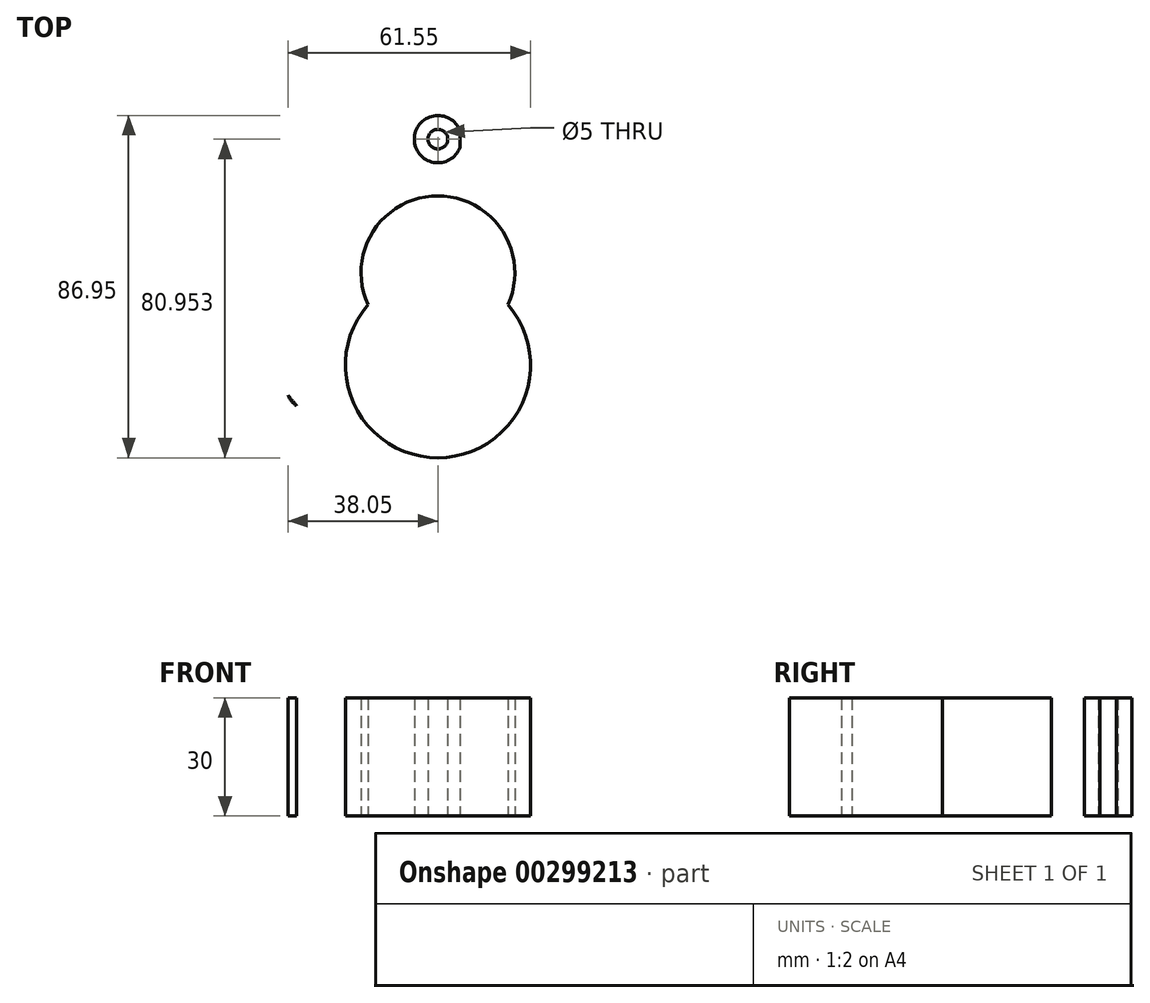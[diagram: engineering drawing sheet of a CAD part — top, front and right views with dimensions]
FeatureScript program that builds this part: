
annotation { "Feature Type Name" : "Feature", "Feature Type Description" : "" }
export const myFeature = defineFeature(function(context is Context, id is Id, definition is map)
    precondition{}
    {
        {
            var Q0;
            Q0=qCreatedBy(makeId("Top.planeOp"),FACE);
            var sketch = newSketch(context, id + "F0", { "sketchPlane" : qUnion([Q0])});
            skCircle(sketch, "E0", {"center": v(0, 0) * mm, "radius": 13 * mm});
            skCircle(sketch, "E1", {"center": v(0, 0) * mm, "radius": 20 * mm});
            skCircle(sketch, "E2", {"center": v(0, 0) * mm, "radius": 23.5 * mm});
            skArc(sketch, "E3", {"start": v(17.77, 15.38) * mm, "mid": v(0, 43.04) * mm, "end": v(-17.77, 15.38) * mm});
            skCircle(sketch, "E4", {"center": v(0, 23.5) * mm, "radius": 14.54 * mm});
            skCircle(sketch, "E5", {"center": v(-32.5, -5.34) * mm, "radius": 6 * mm});
            skPoint(sketch, "E6.orphan", {"position": v(0, -7.55) * mm});
            skCircle(sketch, "E7", {"center": v(-32.5, -5.34) * mm, "radius": 2.5 * mm});
            skCircle(sketch, "E8", {"center": v(32.5, -5.69) * mm, "radius": 6 * mm});
            skCircle(sketch, "E9", {"center": v(32.5, -5.69) * mm, "radius": 2.5 * mm});
            skCircle(sketch, "E10", {"center": v(0, 57.45) * mm, "radius": 6 * mm});
            skCircle(sketch, "E11", {"center": v(0, 57.45) * mm, "radius": 2.5 * mm});
            skLineSegment(sketch, "E12", {"start": v(5.6, 59.59) * mm, "end": v(5.6, 42.22) * mm});
            skLineSegment(sketch, "E13", {"start": v(-6, 57.45) * mm, "end": v(-6, 42.1) * mm});
            skLineSegment(sketch, "E14", {"start": v(-32.5, -5.34) * mm, "end": v(-30.84, -5.69) * mm, "construction": true});
            skLineSegment(sketch, "E15", {"start": v(42.3, 57.45) * mm, "end": v(-57.95, 57.45) * mm, "construction": true});
            skLineSegment(sketch, "E16", {"start": v(-2.13, 23.5) * mm, "end": v(-57.13, 23.5) * mm, "construction": true});
            skArc(sketch, "E17", {"start": v(-26.82, 24) * mm, "mid": v(-29.6, 19.39) * mm, "end": v(-30.2, 14.03) * mm});
            skLineSegment(sketch, "E18", {"start": v(-5.18, 60.47) * mm, "end": v(-26.82, 24) * mm});
            skLineSegment(sketch, "E19", {"start": v(5.6, 60.47) * mm, "end": v(28.74, 26.8) * mm});
            skLineSegment(sketch, "E20", {"start": v(-30.2, 14.03) * mm, "end": v(-37.95, -2.83) * mm});
            skLineSegment(sketch, "E21", {"start": v(31.53, 14.03) * mm, "end": v(38.12, -3.59) * mm});
            skArc(sketch, "E22", {"start": v(-38.05, -7.6) * mm, "mid": v(0.8, -26.3) * mm, "end": v(38.49, -5.34) * mm});
            skArc(sketch, "E23.trimOffspring", {"start": v(-7.37, 22.31) * mm, "mid": v(-7.8, 22.92) * mm, "end": v(-8.27, 23.5) * mm});
            skArc(sketch, "E24.trimOffspring", {"start": v(31.53, 14.03) * mm, "mid": v(31.93, 20.81) * mm, "end": v(28.74, 26.8) * mm});
            skLineSegment(sketch, "E25", {"start": v(-32.5, -11.34) * mm, "end": v(-20.59, -11.34) * mm});
            skLineSegment(sketch, "E26", {"start": v(-30.84, 0) * mm, "end": v(-23.5, 0) * mm});
            skLineSegment(sketch, "E27", {"start": v(30.6, 0) * mm, "end": v(23.5, 0) * mm});
            skLineSegment(sketch, "E28", {"start": v(30.47, -11.34) * mm, "end": v(20.59, -11.34) * mm});
            skSolve(sketch);
        }
        {
            var Q0;
            {var subQ0=sQuery(id+"F0.wireOp",EDGE,"E22");var subQ1=sQuery(id+"F0.wireOp",EDGE,"E5");var subQ2=makeQuery(id+"F0.imprint","INTERSECT",VERTEX,{"disambiguationData":[OD(0.0)],"derivedFrom":[subQ1,subQ0]});Q0=makeQuery(id+"F0.imprint","IMPRINT",FACE,{"disambiguationData":[TD([[makeQuery(id+"F0.imprint","IMPRINT",EDGE,{"disambiguationData":[TD([[subQ2,-1.0]])],"derivedFrom":subQ1}),1.0]])]});}
            var Q1;
            {var subQ0=sQuery(id+"F0.wireOp",EDGE,"E12");var subQ1=sQuery(id+"F0.wireOp",EDGE,"E10");var subQ2=makeQuery(id+"F0.imprint","INTERSECT",VERTEX,{"disambiguationData":[OD(0.0)],"derivedFrom":[subQ1,subQ0]});Q1=makeQuery(id+"F0.imprint","IMPRINT",FACE,{"disambiguationData":[TD([[makeQuery(id+"F0.imprint","IMPRINT",EDGE,{"disambiguationData":[TD([[subQ2,1.0]])],"derivedFrom":subQ1}),1.0]])]});}
            var Q2;
            {var subQ0=sQuery(id+"F0.wireOp",EDGE,"E3");var subQ3=sQuery(id+"F0.wireOp",EDGE,"E2");var subQ4=makeQuery(id+"F0.imprint","INTERSECT",VERTEX,{"disambiguationData":[OD(0.0)],"derivedFrom":[subQ3,subQ0]});Q2=makeQuery(id+"F0.imprint","IMPRINT",FACE,{"disambiguationData":[TD([[makeQuery(id+"F0.imprint","IMPRINT",EDGE,{"disambiguationData":[TD([[subQ4,-1.0]])],"derivedFrom":subQ3}),-1.0]])]});}
            var Q3;
            {var subQ3=sQuery(id+"F0.wireOp",EDGE,"E4");var subQ5=sQuery(id+"F0.wireOp",EDGE,"E1");var subQ6=makeQuery(id+"F0.imprint","INTERSECT",VERTEX,{"disambiguationData":[OD(0.0)],"derivedFrom":[subQ5,subQ3]});Q3=makeQuery(id+"F0.imprint","IMPRINT",FACE,{"disambiguationData":[TD([[makeQuery(id+"F0.imprint","IMPRINT",EDGE,{"disambiguationData":[TD([[subQ6,-1.0]])],"derivedFrom":subQ5}),-1.0]])]});}
            var Q4;
            {var subQ0=sQuery(id+"F0.wireOp",EDGE,"E2");var subQ1=makeQuery(id+"F0.imprint","IMPRINT",VERTEX,{"derivedFrom":subQ0});Q4=makeQuery(id+"F0.imprint","IMPRINT",FACE,{"disambiguationData":[TD([[makeQuery(id+"F0.imprint","IMPRINT",EDGE,{"disambiguationData":[TD([[subQ1,1.0]])],"derivedFrom":subQ0}),-1.0]])]});}
            var Q5;
            {var subQ3=sQuery(id+"F0.wireOp",EDGE,"E2");var subQ5=makeQuery(id+"F0.imprint","IMPRINT",VERTEX,{"derivedFrom":subQ3});Q5=makeQuery(id+"F0.imprint","IMPRINT",FACE,{"disambiguationData":[TD([[makeQuery(id+"F0.imprint","IMPRINT",EDGE,{"disambiguationData":[TD([[subQ5,1.0]])],"derivedFrom":subQ3}),1.0]])]});}
            var Q6;
            {var subQ0=sQuery(id+"F0.wireOp",EDGE,"E4");var subQ1=sQuery(id+"F0.wireOp",EDGE,"E0");var subQ2=makeQuery(id+"F0.imprint","INTERSECT",VERTEX,{"disambiguationData":[OD(0.0)],"derivedFrom":[subQ1,subQ0]});Q6=makeQuery(id+"F0.imprint","IMPRINT",FACE,{"disambiguationData":[TD([[makeQuery(id+"F0.imprint","IMPRINT",EDGE,{"disambiguationData":[TD([[subQ2,1.0]])],"derivedFrom":subQ1}),-1.0]])]});}
            var Q7;
            {var subQ0=sQuery(id+"F0.wireOp",EDGE,"E4");var subQ1=sQuery(id+"F0.wireOp",EDGE,"E0");var subQ2=makeQuery(id+"F0.imprint","INTERSECT",VERTEX,{"disambiguationData":[OD(0.0)],"derivedFrom":[subQ1,subQ0]});Q7=makeQuery(id+"F0.imprint","IMPRINT",FACE,{"disambiguationData":[TD([[makeQuery(id+"F0.imprint","IMPRINT",EDGE,{"disambiguationData":[TD([[subQ2,1.0]])],"derivedFrom":subQ1}),1.0]])]});}
            var Q8;
            {var subQ0=sQuery(id+"F0.wireOp",EDGE,"E4");var subQ1=sQuery(id+"F0.wireOp",EDGE,"E0");var subQ2=makeQuery(id+"F0.imprint","INTERSECT",VERTEX,{"disambiguationData":[OD(0.0)],"derivedFrom":[subQ1,subQ0]});Q8=makeQuery(id+"F0.imprint","IMPRINT",FACE,{"disambiguationData":[TD([[makeQuery(id+"F0.imprint","IMPRINT",EDGE,{"disambiguationData":[TD([[subQ2,-1.0]])],"derivedFrom":subQ1}),1.0]])]});}
            var Q9;
            {var subQ0=sQuery(id+"F0.wireOp",EDGE,"E4");var subQ1=sQuery(id+"F0.wireOp",EDGE,"E0");var subQ2=makeQuery(id+"F0.imprint","INTERSECT",VERTEX,{"disambiguationData":[OD(0.0)],"derivedFrom":[subQ1,subQ0]});Q9=makeQuery(id+"F0.imprint","IMPRINT",FACE,{"disambiguationData":[TD([[makeQuery(id+"F0.imprint","IMPRINT",EDGE,{"disambiguationData":[TD([[subQ2,-1.0]])],"derivedFrom":subQ1}),-1.0]])]});}
            extrude(context, id + "F1", {"entities" : qUnion([Q0, Q1, Q2, Q3, Q4, Q5, Q6, Q7, Q8, Q9]), "depth" : 30 * mm});
        }
    });
